# Revit family: Lighting-Pendant-Cooper-Shaper-749
name_source: partatom
category: Lighting Fixtures
revit_build: Autodesk Revit 2015 (Build: 20140606_1530(x64)
units: mm (PartAtom-declared; Revit-internal decimal feet)

## types (4) — shared parameters
120 Volt = Yes
277 Volt = No
Apparent Load = 0 VA
Assembly Code = D5020
Color Filter = 16777215
Default Elevation = 0' - 0"
Depth = 0' - 6 1/4"
Description = Small Scale Decorative Pendant Downlight
Dimming Lamp Color Temperature Shift = <None>
Electrical Connector Description = Power In
Emit Shape Visible in Rendering = No
Emit from Circle Diameter = 0' - 5"
Frame Material = Metal - Cooper Industries - Aluminum Paint
Lamp = Lamp
Length = 0' - 5"
Manufacturer = Cooper Lighting
Model = 749
Number of Poles = 1
Product data url = https://bimobject.com
Tilt Angle = 90.00°
Total Input Wattage = 0 W
Type Comments = Legacy 749 Series
URL = www.eaton.com/lighting
Voltage = 120 V
Width = 0' - 5"
zero-valued in all types: Power Factor

## per-type parameters (varying)
| type | Photometric Web File | Product Page URL |
| 2700 K | Select File | http://www.cooperindustries.com |
| 3000 K | 749-PSJ-L1_830.IES |  |
| 3500 K | Select File |  |
| 4000 K | Select File |  |

## geometry (parser evidence)
native form markers: Sweep x2
no freeform markers — native parametric forms only
